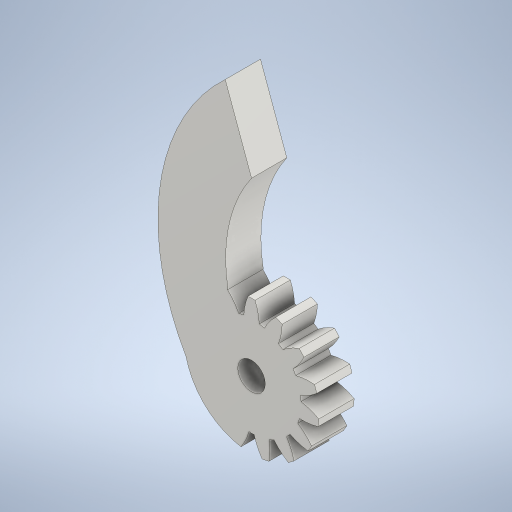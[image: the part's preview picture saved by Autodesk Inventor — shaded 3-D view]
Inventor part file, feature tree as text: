
AUTODESK INVENTOR PART (.ipt)
format: ipt  version: 2024 (Build 280153000, 153)  size: 814,592 bytes
history: native  units: mm (DEFAULTED — no unit token found)
features: extrude x3, plane x3, other x3, sketch x3, projected_geometry x1
ambient origin geometry x8: Origin, YZ Plane, XZ Plane, XY Plane, X Axis, Y Axis, Z Axis, Center Point
bodies: Solid1 (feature_tree)
feature tree (13):
  extrude  "Extrusion1"  Depth=6.666667mm TaperAngle=0.0deg
  plane  "Work Plane2"
  plane  "Work Plane8"
  plane  "Work Plane9"
  other  "Spur Gear"
  extrude  "Extrusion2"  Depth=10.0mm TaperAngle=0.0deg
  extrude  "Extrusion4"  Depth=10.0mm TaperAngle=0.0deg
  sketch  "Sketch1"  dims[d0=25.492855mm d1=6.666667mm d2=0.0mm]
  other  "Srf1"
  sketch  "Sketch3"  dims[d3=22.5mm d4=10.0mm d5=0.0mm]
  sketch  "Sketch7"  dims[d16=23.4mm d17=0.0mm d34=2.094395mm d39=0.0mm d41=0.0mm d43=23.4mm d46=23.4mm d47=0.0mm d48=0.0mm d49=5.2mm d50=10.0mm d51=0.0mm d64=50.0mm d68=54.037661mm d69=22.118mm d70=16.88mm d71=79.653868mm d72=3.490659mm d73=10.0mm d74=0.0mm]
  projected_geometry  "Projected Loop2"
  other  "Pitch Diameter"
